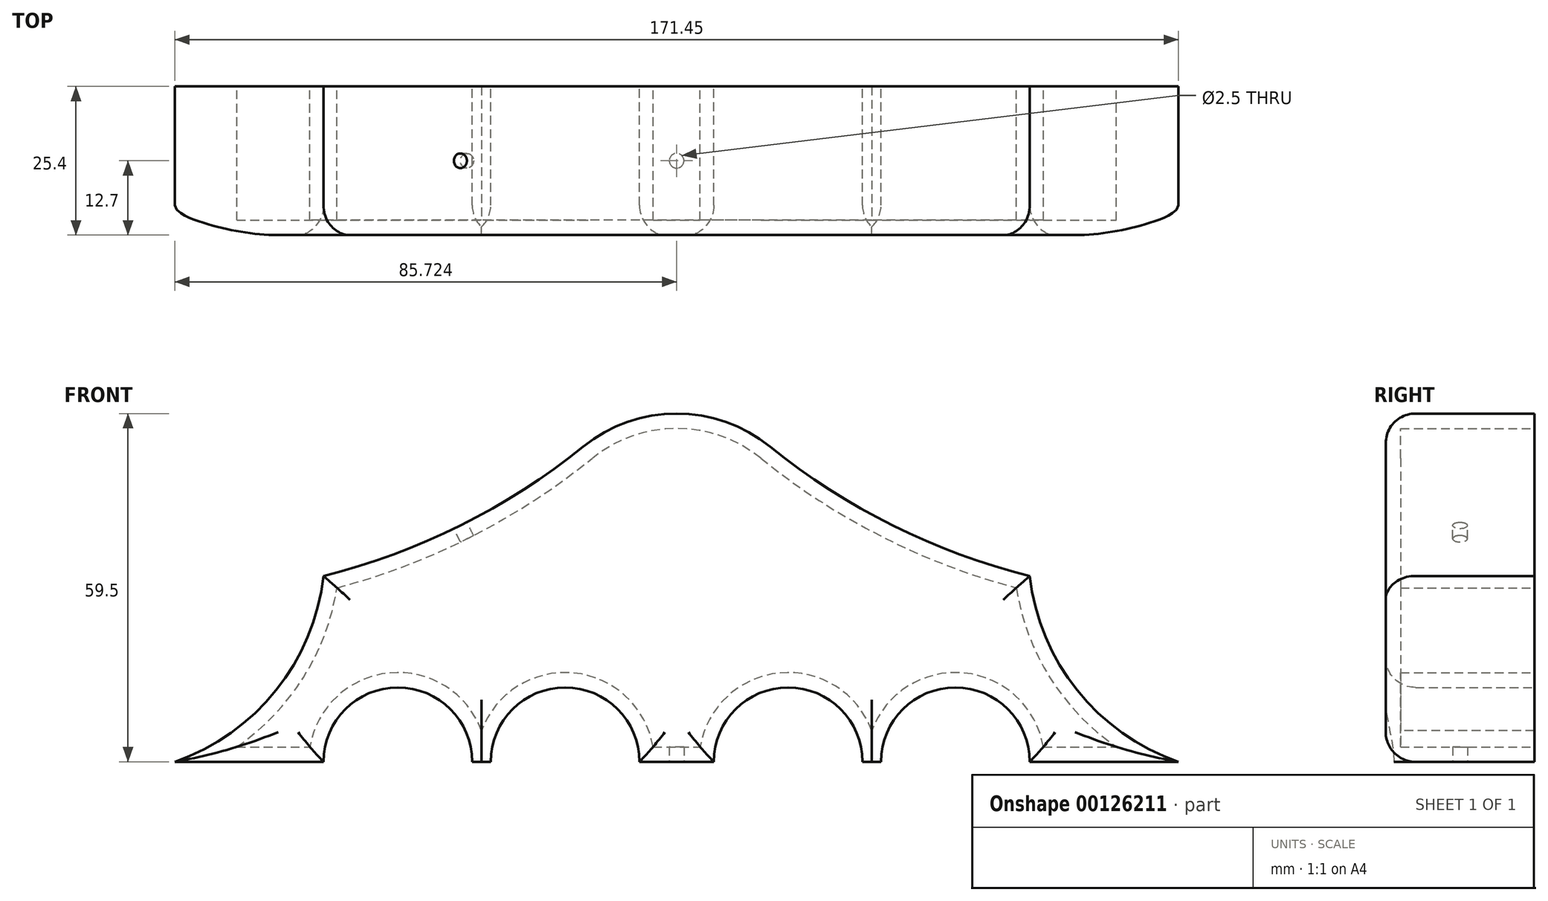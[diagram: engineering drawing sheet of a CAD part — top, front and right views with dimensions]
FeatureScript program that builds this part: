
annotation { "Feature Type Name" : "Feature", "Feature Type Description" : "" }
export const myFeature = defineFeature(function(context is Context, id is Id, definition is map)
    precondition{}
    {
        {
            var Q0;
            Q0=qCreatedBy(makeId("Front.planeOp"),FACE);
            var sketch = newSketch(context, id + "F0", { "sketchPlane" : qUnion([Q0])});
            skLineSegment(sketch, "E0", {"start": v(-75.43, -35.56) * mm, "end": v(-50.03, -35.56) * mm});
            skLineSegment(sketch, "E1", {"start": v(-24.63, -35.56) * mm, "end": v(-21.46, -35.56) * mm});
            skLineSegment(sketch, "E2", {"start": v(3.94, -35.56) * mm, "end": v(16.64, -35.56) * mm});
            skLineSegment(sketch, "E3", {"start": v(42.04, -35.56) * mm, "end": v(45.22, -35.56) * mm});
            skLineSegment(sketch, "E4", {"start": v(70.62, -35.56) * mm, "end": v(96.02, -35.56) * mm});
            skArc(sketch, "E5", {"start": v(-24.63, -35.56) * mm, "mid": v(-37.33, -22.86) * mm, "end": v(-50.03, -35.56) * mm});
            skArc(sketch, "E6", {"start": v(3.94, -35.56) * mm, "mid": v(-8.76, -22.86) * mm, "end": v(-21.46, -35.56) * mm});
            skArc(sketch, "E7", {"start": v(42.04, -35.56) * mm, "mid": v(29.34, -22.86) * mm, "end": v(16.64, -35.56) * mm});
            skArc(sketch, "E8", {"start": v(70.62, -35.56) * mm, "mid": v(57.92, -22.86) * mm, "end": v(45.22, -35.56) * mm});
            skArc(sketch, "E9", {"start": v(-75.43, -35.56) * mm, "mid": v(-58.14, -23.35) * mm, "end": v(-50.03, -3.8) * mm});
            skArc(sketch, "E10", {"start": v(70.62, -3.8) * mm, "mid": v(78.73, -23.35) * mm, "end": v(96.02, -35.56) * mm});
            skArc(sketch, "E11", {"start": v(-50.03, -3.8) * mm, "mid": v(-26.65, 4.8) * mm, "end": v(-5.69, 18.28) * mm});
            skPoint(sketch, "E11.endSnap0", {"position": v(10.3, -35.56) * mm});
            skArc(sketch, "E12", {"start": v(26.28, 18.28) * mm, "mid": v(47.24, 4.8) * mm, "end": v(70.62, -3.8) * mm});
            skPoint(sketch, "E13.visualSharp", {"position": v(10.3, 34.06) * mm});
            skArc(sketch, "E13.filletArc", {"start": v(26.28, 18.28) * mm, "mid": v(10.3, 23.94) * mm, "end": v(-5.69, 18.28) * mm});
            skSolve(sketch);
        }
        {
            var Q0;
            Q0=makeQuery(id+"F0.imprint","IMPRINT",FACE,{"disambiguationData":[TD([[makeQuery(id+"F0.imprint","IMPRINT",EDGE,{"derivedFrom":sQuery(id+"F0.wireOp",EDGE,"E0")}),1.0]])]});
            extrude(context, id + "F1", {"entities" : qUnion([Q0]), "depth" : 25.4 * mm});
        }
        {
            var Q0;
            Q0=makeQuery(id+"F1.opExtrude","CAP_FACE",FACE,{"disambiguationData":[OSD([sQuery(id+"F0.wireOp",EDGE,"E0"),sQuery(id+"F0.wireOp",EDGE,"E1"),sQuery(id+"F0.wireOp",EDGE,"E2"),sQuery(id+"F0.wireOp",EDGE,"E3"),sQuery(id+"F0.wireOp",EDGE,"E4"),sQuery(id+"F0.wireOp",EDGE,"E5"),sQuery(id+"F0.wireOp",EDGE,"E6"),sQuery(id+"F0.wireOp",EDGE,"E7"),sQuery(id+"F0.wireOp",EDGE,"E8"),sQuery(id+"F0.wireOp",EDGE,"E9"),sQuery(id+"F0.wireOp",EDGE,"E10"),sQuery(id+"F0.wireOp",EDGE,"E11"),sQuery(id+"F0.wireOp",EDGE,"E12"),sQuery(id+"F0.wireOp",EDGE,"E13.filletArc")])],"isStart":true});
            shell(context, id + "F2", {"entities" : qUnion([Q0]), "thickness" : 2.54 * mm});
        }
        {
            var Q0;
            Q0=makeQuery(id+"F1.opExtrude","SWEPT_FACE",FACE,{"disambiguationData":[OSD([sQuery(id+"F0.wireOp",EDGE,"E2")])]});
            var sketch = newSketch(context, id + "F3", { "sketchPlane" : qUnion([Q0])});
            skLineSegment(sketch, "E14", {"start": v(3.94, 12.7) * mm, "end": v(16.64, 12.7) * mm, "construction": true});
            skCircle(sketch, "E15", {"center": v(10.3, 12.7) * mm, "radius": 1.25 * mm});
            skSolve(sketch);
        }
        {
            var Q0;
            Q0=makeQuery(id+"F3.imprint","IMPRINT",FACE,{"disambiguationData":[TD([[makeQuery(id+"F3.imprint","IMPRINT",EDGE,{"derivedFrom":sQuery(id+"F3.wireOp",EDGE,"E15")}),1.0]])]});
            var Q1;
            Q1=makeQuery(id+"F2.opShell","OFFSET_FACE",FACE,{"disambiguationData":[OSD([sQuery(id+"F0.wireOp",EDGE,"E2")])]});
            extrude(context, id + "F4", {"entities" : qUnion([Q0]), "operationType" : NewBodyOperationType.REMOVE, "endBound" : BoundingType.UP_TO_SURFACE, "oppositeDirection" : true, "endBoundEntityFace" : qUnion([Q1]), "depth" : 25.4 * mm});
        }
        {
            var Q0;
            Q0=makeQuery(id+"F1.opExtrude","CAP_FACE",FACE,{"disambiguationData":[OSD([sQuery(id+"F0.wireOp",EDGE,"E0"),sQuery(id+"F0.wireOp",EDGE,"E1"),sQuery(id+"F0.wireOp",EDGE,"E2"),sQuery(id+"F0.wireOp",EDGE,"E3"),sQuery(id+"F0.wireOp",EDGE,"E4"),sQuery(id+"F0.wireOp",EDGE,"E5"),sQuery(id+"F0.wireOp",EDGE,"E6"),sQuery(id+"F0.wireOp",EDGE,"E7"),sQuery(id+"F0.wireOp",EDGE,"E8"),sQuery(id+"F0.wireOp",EDGE,"E9"),sQuery(id+"F0.wireOp",EDGE,"E10"),sQuery(id+"F0.wireOp",EDGE,"E11"),sQuery(id+"F0.wireOp",EDGE,"E12"),sQuery(id+"F0.wireOp",EDGE,"E13.filletArc")])],"isStart":true});
            var sketch = newSketch(context, id + "F5", { "sketchPlane" : qUnion([Q0])});
            skLineSegment(sketch, "E16", {"start": v(50.03, -3.8) * mm, "end": v(5.69, 18.28) * mm, "construction": true});
            skSolve(sketch);
        }
        {
            var Q0;
            Q0=makeQuery(id+"F1.opExtrude","CAP_FACE",FACE,{"disambiguationData":[OSD([sQuery(id+"F0.wireOp",EDGE,"E0"),sQuery(id+"F0.wireOp",EDGE,"E1"),sQuery(id+"F0.wireOp",EDGE,"E2"),sQuery(id+"F0.wireOp",EDGE,"E3"),sQuery(id+"F0.wireOp",EDGE,"E4"),sQuery(id+"F0.wireOp",EDGE,"E5"),sQuery(id+"F0.wireOp",EDGE,"E6"),sQuery(id+"F0.wireOp",EDGE,"E7"),sQuery(id+"F0.wireOp",EDGE,"E8"),sQuery(id+"F0.wireOp",EDGE,"E9"),sQuery(id+"F0.wireOp",EDGE,"E10"),sQuery(id+"F0.wireOp",EDGE,"E11"),sQuery(id+"F0.wireOp",EDGE,"E12"),sQuery(id+"F0.wireOp",EDGE,"E13.filletArc")])],"isStart":false});
            var sketch = newSketch(context, id + "F6", { "sketchPlane" : qUnion([Q0])});
            skLineSegment(sketch, "E17", {"start": v(-50.03, -3.8) * mm, "end": v(-5.69, 18.28) * mm, "construction": true});
            skSolve(sketch);
        }
        {
            var Q0;
            Q0=sQuery(id+"F6.wireOp",EDGE,"E17");
            cPlane(context, id + "F7", {"entities" : qUnion([Q0]), "cplaneType" : CPlaneType.LINE_ANGLE, "offset" : 25.4 * mm, "angle" : 90 * degree, "width" : 152.4 * mm, "height" : 152.4 * mm});
        }
        {
            var Q0;
            Q0=qCreatedBy(id+"F7.planeOp",FACE);
            var sketch = newSketch(context, id + "F8", { "sketchPlane" : qUnion([Q0])});
            skLineSegment(sketch, "E18.0", {"start": v(-46.48, -25.4) * mm, "end": v(-46.48, 0) * mm});
            skLineSegment(sketch, "E19.0", {"start": v(-46.48, -25.4) * mm, "end": v(3.06, -25.4) * mm});
            skLineSegment(sketch, "E20.0", {"start": v(-46.48, 0) * mm, "end": v(3.06, 0) * mm});
            skLineSegment(sketch, "E21.0", {"start": v(3.06, -25.4) * mm, "end": v(3.06, 0) * mm});
            skCircle(sketch, "E22", {"center": v(-21.71, -12.7) * mm, "radius": 1.25 * mm});
            skPoint(sketch, "E22.centerSnap0", {"position": v(-46.48, -12.7) * mm});
            skPoint(sketch, "E22.centerSnap1", {"position": v(-21.71, 0) * mm});
            skSolve(sketch);
        }
        {
            var Q0;
            Q0=makeQuery(id+"F8.imprint","IMPRINT",FACE,{"disambiguationData":[TD([[makeQuery(id+"F8.imprint","IMPRINT",EDGE,{"derivedFrom":sQuery(id+"F8.wireOp",EDGE,"E22")}),1.0]])]});
            var Q1;
            Q1=makeQuery(id+"F2.opShell","OFFSET_FACE",FACE,{"disambiguationData":[OSD([sQuery(id+"F0.wireOp",EDGE,"E11")])]});
            extrude(context, id + "F9", {"entities" : qUnion([Q0]), "operationType" : NewBodyOperationType.REMOVE, "endBound" : BoundingType.UP_TO_SURFACE, "oppositeDirection" : true, "endBoundEntityFace" : qUnion([Q1]), "depth" : 25.4 * mm});
        }
        {
            var Q0;
            Q0=makeQuery(id+"F1.opExtrude","CAP_EDGE",EDGE,{"disambiguationData":[OSD([sQuery(id+"F0.wireOp",EDGE,"E10")])],"isStart":false});
            var Q1;
            Q1=makeQuery(id+"F1.opExtrude","CAP_EDGE",EDGE,{"disambiguationData":[OSD([sQuery(id+"F0.wireOp",EDGE,"E12")])],"isStart":false});
            var Q2;
            Q2=makeQuery(id+"F1.opExtrude","CAP_EDGE",EDGE,{"disambiguationData":[OSD([sQuery(id+"F0.wireOp",EDGE,"E9")])],"isStart":false});
            var Q3;
            Q3=makeQuery(id+"F1.opExtrude","CAP_EDGE",EDGE,{"disambiguationData":[OSD([sQuery(id+"F0.wireOp",EDGE,"E8")])],"isStart":false});
            var Q4;
            Q4=makeQuery(id+"F1.opExtrude","CAP_EDGE",EDGE,{"disambiguationData":[OSD([sQuery(id+"F0.wireOp",EDGE,"E7")])],"isStart":false});
            var Q5;
            Q5=makeQuery(id+"F1.opExtrude","CAP_EDGE",EDGE,{"disambiguationData":[OSD([sQuery(id+"F0.wireOp",EDGE,"E6")])],"isStart":false});
            var Q6;
            Q6=makeQuery(id+"F1.opExtrude","CAP_EDGE",EDGE,{"disambiguationData":[OSD([sQuery(id+"F0.wireOp",EDGE,"E5")])],"isStart":false});
            var Q7;
            Q7=makeQuery(id+"F1.opExtrude","CAP_EDGE",EDGE,{"disambiguationData":[OSD([sQuery(id+"F0.wireOp",EDGE,"E4")])],"isStart":false});
            var Q8;
            Q8=makeQuery(id+"F1.opExtrude","CAP_EDGE",EDGE,{"disambiguationData":[OSD([sQuery(id+"F0.wireOp",EDGE,"E2")])],"isStart":false});
            var Q9;
            Q9=makeQuery(id+"F1.opExtrude","CAP_EDGE",EDGE,{"disambiguationData":[OSD([sQuery(id+"F0.wireOp",EDGE,"E3")])],"isStart":false});
            var Q10;
            Q10=makeQuery(id+"F1.opExtrude","CAP_EDGE",EDGE,{"disambiguationData":[OSD([sQuery(id+"F0.wireOp",EDGE,"E1")])],"isStart":false});
            var Q11;
            Q11=makeQuery(id+"F1.opExtrude","CAP_EDGE",EDGE,{"disambiguationData":[OSD([sQuery(id+"F0.wireOp",EDGE,"E0")])],"isStart":false});
            fillet(context, id + "F10", {"entities" : qUnion([Q0, Q1, Q2, Q3, Q4, Q5, Q6, Q7, Q8, Q9, Q10, Q11]), "radius" : 5.08 * mm, "tangentPropagation" : true, "allowEdgeOverflow" : false});
        }
    });
